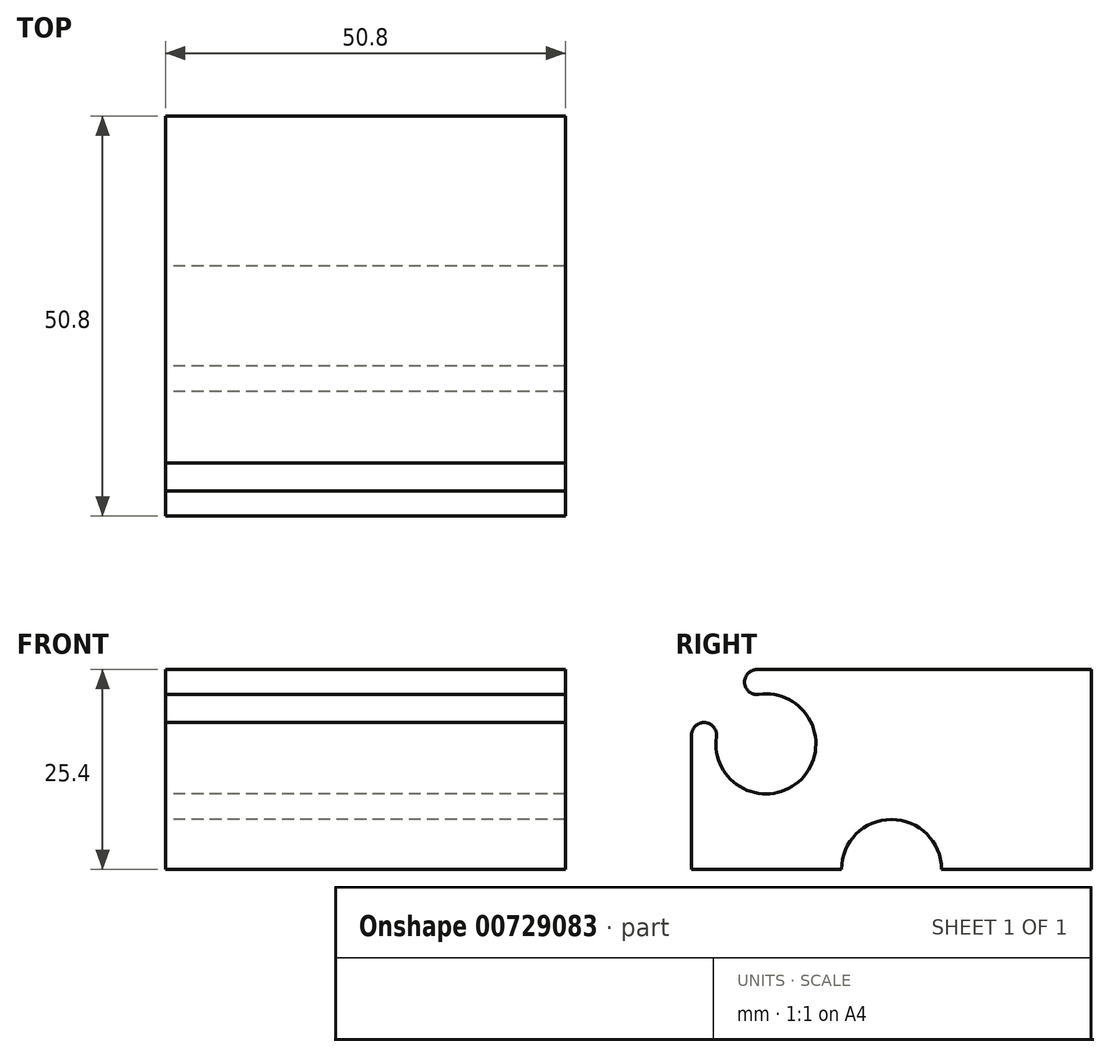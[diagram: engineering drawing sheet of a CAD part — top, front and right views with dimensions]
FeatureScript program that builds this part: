
annotation { "Feature Type Name" : "Feature", "Feature Type Description" : "" }
export const myFeature = defineFeature(function(context is Context, id is Id, definition is map)
    precondition{}
    {
        {
            var Q0;
            Q0=qCreatedBy(makeId("Right.planeOp"),FACE);
            var sketch = newSketch(context, id + "F0", { "sketchPlane" : qUnion([Q0])});
            skArc(sketch, "E0", {"start": v(-6.29, 0.9) * mm, "mid": v(4.5, -4.5) * mm, "end": v(-0.9, 6.29) * mm});
            skLineSegment(sketch, "E1", {"start": v(-1.12, 9.45) * mm, "end": v(41.35, 9.45) * mm});
            skLineSegment(sketch, "E2", {"start": v(41.35, 9.45) * mm, "end": v(41.35, -15.95) * mm});
            skLineSegment(sketch, "E3", {"start": v(41.35, -15.95) * mm, "end": v(22.3, -15.95) * mm});
            skArc(sketch, "E4", {"start": v(22.3, -15.95) * mm, "mid": v(15.95, -9.6) * mm, "end": v(9.6, -15.95) * mm});
            skLineSegment(sketch, "E5", {"start": v(9.6, -15.95) * mm, "end": v(-9.45, -15.95) * mm});
            skLineSegment(sketch, "E6", {"start": v(-9.45, -15.95) * mm, "end": v(-9.45, 1.12) * mm});
            skArc(sketch, "E7.filletArc", {"start": v(-1.12, 9.45) * mm, "mid": v(-2.7, 7.75) * mm, "end": v(-0.9, 6.29) * mm});
            skArc(sketch, "E8", {"start": v(-6.29, 0.9) * mm, "mid": v(-7.75, 2.7) * mm, "end": v(-9.45, 1.12) * mm});
            skLineSegment(sketch, "E9", {"start": v(-7.86, 1.12) * mm, "end": v(-1.12, 7.86) * mm, "construction": true});
            skLineSegment(sketch, "E10", {"start": v(0, 0) * mm, "end": v(-4.5, 4.5) * mm, "construction": true});
            skSolve(sketch);
        }
        {
            var Q0;
            Q0=makeQuery(id+"F0.imprint","IMPRINT",FACE,{"disambiguationData":[TD([[makeQuery(id+"F0.imprint","IMPRINT",EDGE,{"derivedFrom":sQuery(id+"F0.wireOp",EDGE,"E0")}),-1.0]])]});
            extrude(context, id + "F1", {"entities" : qUnion([Q0]), "endBound" : BoundingType.SYMMETRIC, "depth" : 50.8 * mm, "offsetDistance" : 25.4 * mm});
        }
    });
